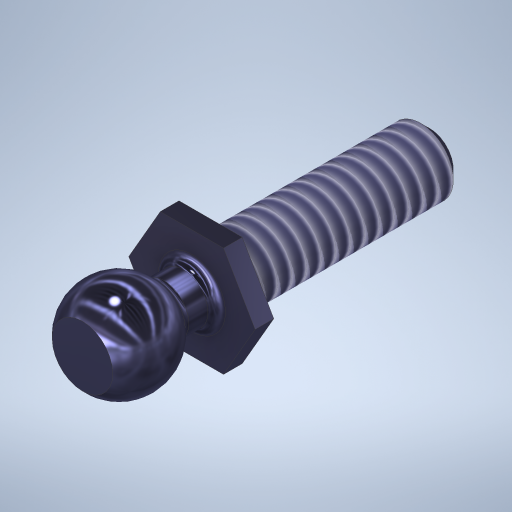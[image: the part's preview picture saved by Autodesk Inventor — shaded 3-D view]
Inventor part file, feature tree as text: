
AUTODESK INVENTOR PART (.ipt)
format: ipt  version: 2023.1 (Build 271208000, 208)  size: 375,808 bytes
history: native  units: in
note: dims shown in document units (in); Inventor stores cm internally (conversion verified against a paired STEP export)
features: sketch x4, extrude x3, revolve x1, fillet x1, plane x1, split x1, chamfer x1, thread x1
ambient origin geometry x8: Origin, YZ Plane, XZ Plane, XY Plane, X Axis, Y Axis, Z Axis, Center Point
bodies: Solid1 (feature_tree)
feature tree (13):
  extrude  "Extrusion1"  Depth=0.032in TaperAngle=0.0deg
  extrude  "Extrusion2"  Depth=0.125in TaperAngle=0.0deg
  revolve  "Revolution1"  Angle=90.0deg
  fillet  "Fillet1"  Radius=0.015in
  plane  "Work Plane1"
  split  "Split1"
  extrude  "Extrusion3"  Depth=0.015in
  chamfer  "Chamfer1"  Distance=0.375in
  thread  "Thread1"  [1 undecoded]
  sketch  "Sketch1"  dims[d0=0.1875in d1=0.032in d2=0.0in]
  sketch  "Sketch2"  dims[d3=0.085in d4=0.125in d5=0.0in]
  sketch  "Sketch3"  dims[d6=0.1625in d7=90.0deg d8=0.015in]
  sketch  "Sketch4"  dims[d9=0.1875in d10=0.112in d11=0.375in d12=0.0in d13=0.015in d14=0.125in d15=45.0deg d16=1.0in d17=0.0in]
note: 1 required parameter value undecoded (feature->parameter linkage not recoverable at this tier; creation-order binding heuristic only, values carry confidence <= 0.55)
